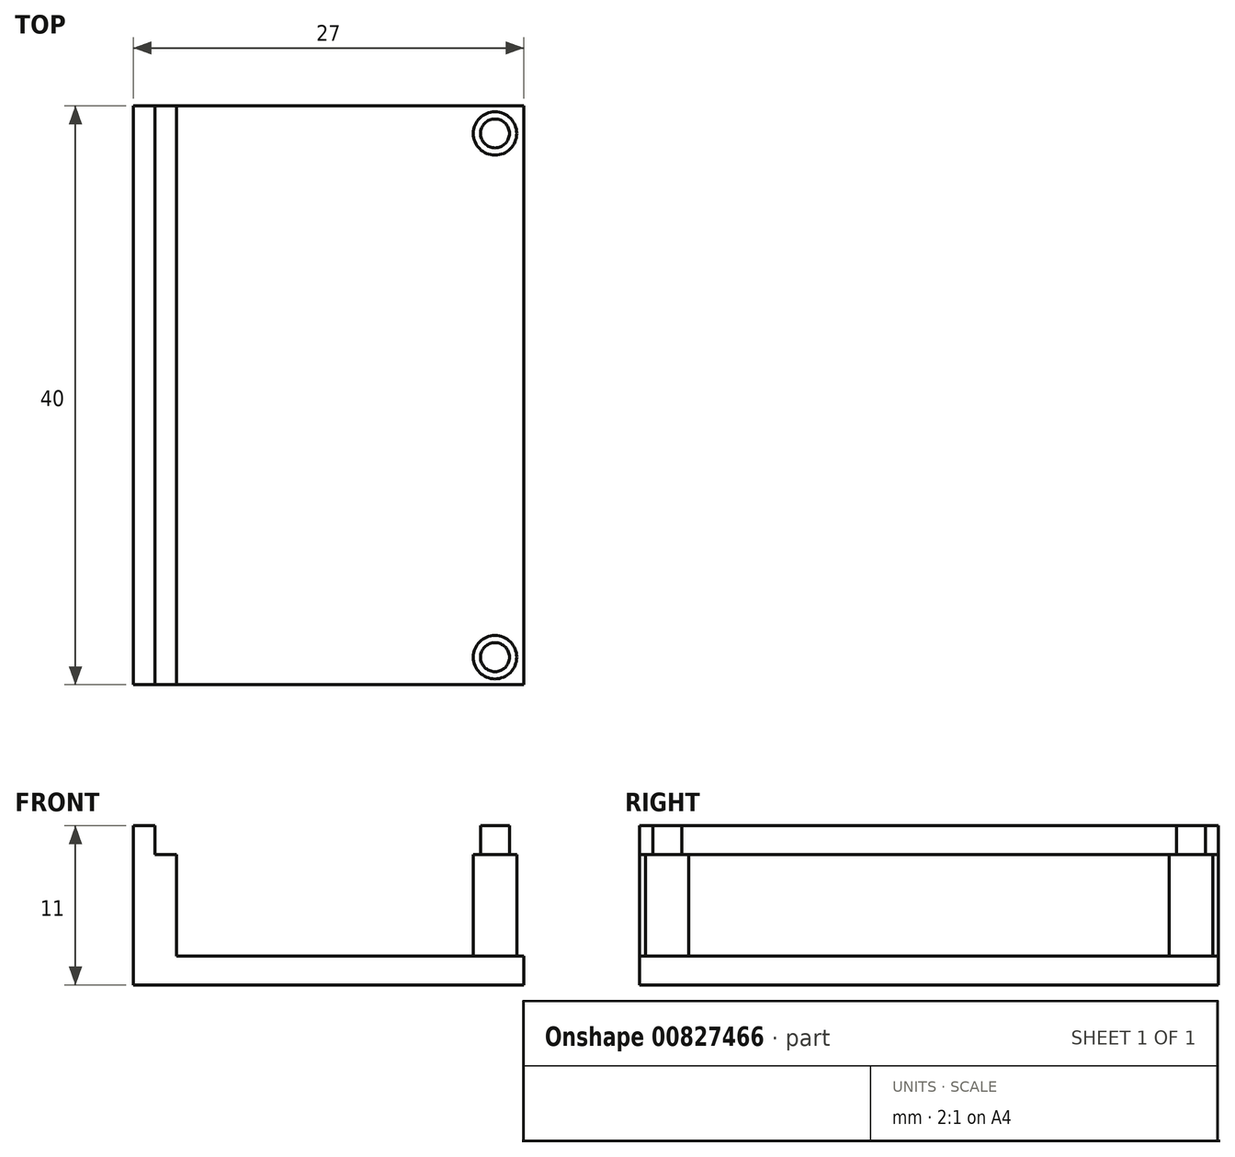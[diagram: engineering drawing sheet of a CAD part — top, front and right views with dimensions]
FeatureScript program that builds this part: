
annotation { "Feature Type Name" : "Feature", "Feature Type Description" : "" }
export const myFeature = defineFeature(function(context is Context, id is Id, definition is map)
    precondition{}
    {
        {
            var Q0;
            Q0=qCreatedBy(makeId("Top.planeOp"),FACE);
            var sketch = newSketch(context, id + "F0", { "sketchPlane" : qUnion([Q0])});
            skLineSegment(sketch, "E0.bottom", {"start": v(-39.24, 22.32) * mm, "end": v(-12.24, 22.32) * mm});
            skLineSegment(sketch, "E0.top", {"start": v(-39.24, -17.68) * mm, "end": v(-12.24, -17.68) * mm});
            skLineSegment(sketch, "E0.left", {"start": v(-39.24, 22.32) * mm, "end": v(-39.24, -17.68) * mm});
            skLineSegment(sketch, "E0.right", {"start": v(-12.24, 22.32) * mm, "end": v(-12.24, -17.68) * mm});
            skCircle(sketch, "E1", {"center": v(-14.24, 20.42) * mm, "radius": 1.5 * mm});
            skCircle(sketch, "E2", {"center": v(-14.24, -15.78) * mm, "radius": 1.5 * mm});
            skLineSegment(sketch, "E3", {"start": v(-14.24, 22.32) * mm, "end": v(-14.24, -17.68) * mm, "construction": true});
            skLineSegment(sketch, "E4", {"start": v(-39.24, 2.32) * mm, "end": v(-12.24, 2.32) * mm, "construction": true});
            skLineSegment(sketch, "E5", {"start": v(-39.24, 2.32) * mm, "end": v(-14.24, 20.42) * mm, "construction": true});
            skLineSegment(sketch, "E6", {"start": v(-39.24, 2.32) * mm, "end": v(-14.24, -15.78) * mm, "construction": true});
            skLineSegment(sketch, "E7", {"start": v(-36.24, 22.32) * mm, "end": v(-36.24, -17.68) * mm});
            skSolve(sketch);
        }
        {
            var Q0;
            Q0=makeQuery(id+"F0.imprint","IMPRINT",FACE,{"disambiguationData":[TD([[makeQuery(id+"F0.imprint","IMPRINT",EDGE,{"derivedFrom":sQuery(id+"F0.wireOp",EDGE,"E0.bottom")}),-1.0]])]});
            var Q1;
            Q1=makeQuery(id+"F0.imprint","IMPRINT",FACE,{"disambiguationData":[TD([[makeQuery(id+"F0.imprint","IMPRINT",EDGE,{"derivedFrom":sQuery(id+"F0.wireOp",EDGE,"E1")}),1.0]])]});
            var Q2;
            Q2=makeQuery(id+"F0.imprint","IMPRINT",FACE,{"disambiguationData":[TD([[makeQuery(id+"F0.imprint","IMPRINT",EDGE,{"derivedFrom":sQuery(id+"F0.wireOp",EDGE,"E2")}),1.0]])]});
            var Q3;
            {var subQ0=sQuery(id+"F0.wireOp",EDGE,"E0.right");Q3=makeQuery(id+"F0.imprint","IMPRINT",FACE,{"disambiguationData":[TD([[makeQuery(id+"F0.imprint","IMPRINT",EDGE,{"derivedFrom":subQ0}),-1.0]])]});}
            extrude(context, id + "F1", {"entities" : qUnion([Q0, Q1, Q2, Q3]), "depth" : 2 * mm, "offsetDistance" : 25 * mm});
        }
        {
            var Q0;
            {var subQ0=sQuery(id+"F0.wireOp",EDGE,"E0.left");Q0=makeQuery(id+"F0.imprint","IMPRINT",FACE,{"disambiguationData":[TD([[makeQuery(id+"F0.imprint","IMPRINT",EDGE,{"derivedFrom":subQ0}),1.0]])]});}
            extrude(context, id + "F2", {"entities" : qUnion([Q0]), "operationType" : NewBodyOperationType.ADD, "depth" : 9 * mm, "offsetDistance" : 25 * mm});
        }
        {
            var Q0;
            Q0=makeQuery(id+"F0.imprint","IMPRINT",FACE,{"disambiguationData":[TD([[makeQuery(id+"F0.imprint","IMPRINT",EDGE,{"derivedFrom":sQuery(id+"F0.wireOp",EDGE,"E1")}),1.0]])]});
            var Q1;
            Q1=makeQuery(id+"F0.imprint","IMPRINT",FACE,{"disambiguationData":[TD([[makeQuery(id+"F0.imprint","IMPRINT",EDGE,{"derivedFrom":sQuery(id+"F0.wireOp",EDGE,"E2")}),1.0]])]});
            var Q2;
            Q2=makeQuery(id+"F2.opExtrude","CAP_FACE",FACE,{"disambiguationData":[OSD([sQuery(id+"F0.wireOp",EDGE,"E0.bottom"),sQuery(id+"F0.wireOp",EDGE,"E0.top"),sQuery(id+"F0.wireOp",EDGE,"E0.left"),sQuery(id+"F0.wireOp",EDGE,"E7")])],"isStart":false});
            extrude(context, id + "F3", {"entities" : qUnion([Q0, Q1]), "operationType" : NewBodyOperationType.ADD, "endBound" : BoundingType.UP_TO_SURFACE, "depth" : 9 * mm, "endBoundEntityFace" : qUnion([Q2]), "offsetDistance" : 25 * mm});
        }
        {
            var Q0;
            Q0=makeQuery(id+"F2.opExtrude","CAP_FACE",FACE,{"disambiguationData":[OSD([sQuery(id+"F0.wireOp",EDGE,"E0.bottom"),sQuery(id+"F0.wireOp",EDGE,"E0.top"),sQuery(id+"F0.wireOp",EDGE,"E0.left"),sQuery(id+"F0.wireOp",EDGE,"E7")])],"isStart":false});
            var sketch = newSketch(context, id + "F4", { "sketchPlane" : qUnion([Q0])});
            skCircle(sketch, "E8.0", {"center": v(-14.24, 20.42) * mm, "radius": 1 * mm});
            skCircle(sketch, "E9.0", {"center": v(-14.24, -15.78) * mm, "radius": 1 * mm});
            skLineSegment(sketch, "E10", {"start": v(-37.74, 22.32) * mm, "end": v(-37.74, -17.68) * mm});
            skSolve(sketch);
        }
        {
            var Q0;
            {var subQ0=sQuery(id+"F4.wireOp",EDGE,"E10");Q0=makeQuery(id+"F4.imprint","IMPRINT",FACE,{"disambiguationData":[TD([[makeQuery(id+"F4.imprint","IMPRINT",EDGE,{"derivedFrom":subQ0}),-1.0]])]});}
            var Q1;
            Q1=makeQuery(id+"F4.imprint","IMPRINT",FACE,{"disambiguationData":[TD([[makeQuery(id+"F4.imprint","IMPRINT",EDGE,{"derivedFrom":sQuery(id+"F4.wireOp",EDGE,"E8.0")}),1.0]])]});
            var Q2;
            Q2=makeQuery(id+"F4.imprint","IMPRINT",FACE,{"disambiguationData":[TD([[makeQuery(id+"F4.imprint","IMPRINT",EDGE,{"derivedFrom":sQuery(id+"F4.wireOp",EDGE,"E9.0")}),1.0]])]});
            extrude(context, id + "F5", {"entities" : qUnion([Q0, Q1, Q2]), "operationType" : NewBodyOperationType.ADD, "depth" : 2 * mm, "offsetDistance" : 25 * mm});
        }
    });
